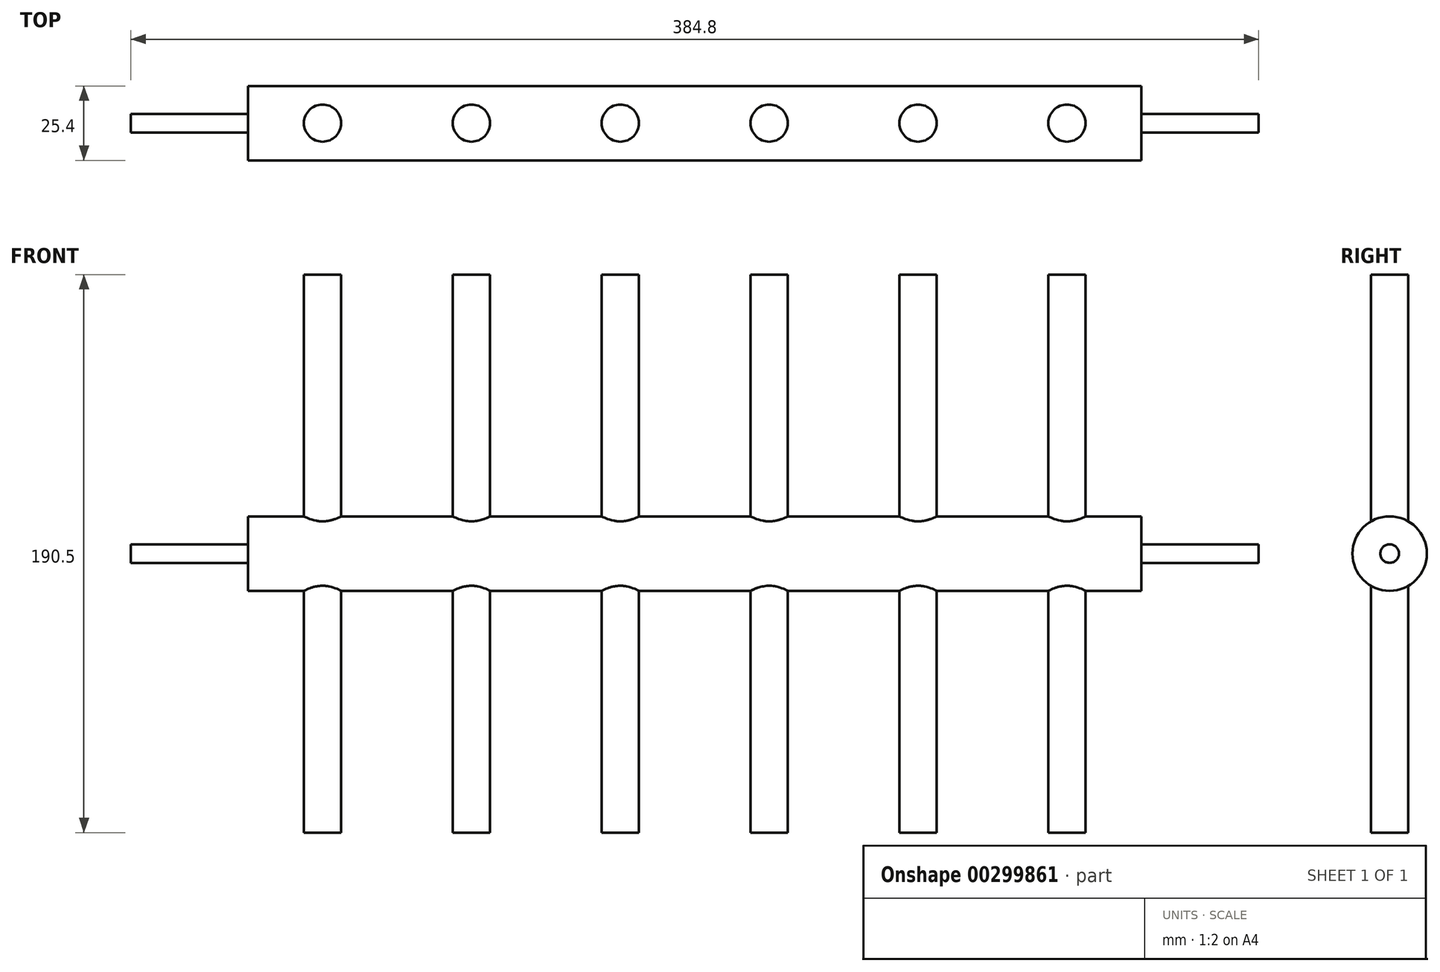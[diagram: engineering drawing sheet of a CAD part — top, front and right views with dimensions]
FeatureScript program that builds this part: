
annotation { "Feature Type Name" : "Feature", "Feature Type Description" : "" }
export const myFeature = defineFeature(function(context is Context, id is Id, definition is map)
    precondition{}
    {
        {
            var Q0;
            Q0=qCreatedBy(makeId("Right.planeOp"),FACE);
            var sketch = newSketch(context, id + "F0", { "sketchPlane" : qUnion([Q0])});
            skCircle(sketch, "E0", {"center": v(0, 0) * mm, "radius": 12.7 * mm});
            skSolve(sketch);
        }
        {
            var Q0;
            Q0=qSketchRegion(id+"F0",true);
            extrude(context, id + "F1", {"entities" : qUnion([Q0]), "depth" : 304.8 * mm});
        }
        {
            var Q0;
            Q0=makeQuery(id+"F1.opExtrude","CAP_FACE",FACE,{"disambiguationData":[OSD([sQuery(id+"F0.wireOp",EDGE,"E0")])],"isStart":false});
            var sketch = newSketch(context, id + "F2", { "sketchPlane" : qUnion([Q0])});
            skCircle(sketch, "E1", {"center": v(0, 0) * mm, "radius": 3.18 * mm});
            skSolve(sketch);
        }
        {
            var Q0;
            Q0=qSketchRegion(id+"F2",true);
            extrude(context, id + "F3", {"entities" : qUnion([Q0]), "operationType" : NewBodyOperationType.ADD, "depth" : 40 * mm});
        }
        {
            var Q0;
            Q0=makeQuery(id+"F1.opExtrude","CAP_FACE",FACE,{"disambiguationData":[OSD([sQuery(id+"F0.wireOp",EDGE,"E0")])],"isStart":true});
            var sketch = newSketch(context, id + "F4", { "sketchPlane" : qUnion([Q0])});
            skCircle(sketch, "E2", {"center": v(0, 0) * mm, "radius": 3.18 * mm});
            skSolve(sketch);
        }
        {
            var Q0;
            Q0=qSketchRegion(id+"F4",true);
            extrude(context, id + "F5", {"entities" : qUnion([Q0]), "operationType" : NewBodyOperationType.ADD, "depth" : 40 * mm});
        }
        {
            var Q0;
            Q0=qCreatedBy(makeId("Top.planeOp"),FACE);
            var sketch = newSketch(context, id + "F6", { "sketchPlane" : qUnion([Q0])});
            skCircle(sketch, "E3", {"center": v(177.8, 0) * mm, "radius": 6.35 * mm});
            skLineSegment(sketch, "E4", {"start": v(177.8, 0) * mm, "end": v(127, 0) * mm});
            skLineSegment(sketch, "E5", {"start": v(127, 0) * mm, "end": v(76.2, 0) * mm});
            skLineSegment(sketch, "E6", {"start": v(76.2, 0) * mm, "end": v(25.4, 0) * mm});
            skLineSegment(sketch, "E7", {"start": v(0, 0) * mm, "end": v(25.4, 0) * mm});
            skLineSegment(sketch, "E8", {"start": v(177.8, 0) * mm, "end": v(228.6, 0) * mm});
            skLineSegment(sketch, "E9", {"start": v(228.6, 0) * mm, "end": v(279.4, 0) * mm});
            skCircle(sketch, "E10", {"center": v(25.4, 0) * mm, "radius": 6.35 * mm});
            skCircle(sketch, "E11", {"center": v(76.2, 0) * mm, "radius": 6.35 * mm});
            skCircle(sketch, "E12", {"center": v(127, 0) * mm, "radius": 6.35 * mm});
            skCircle(sketch, "E13", {"center": v(228.6, 0) * mm, "radius": 6.35 * mm});
            skCircle(sketch, "E14", {"center": v(279.4, 0) * mm, "radius": 6.35 * mm});
            skSolve(sketch);
        }
        {
            var Q0;
            Q0=qSketchRegion(id+"F6",true);
            extrude(context, id + "F7", {"entities" : qUnion([Q0]), "operationType" : NewBodyOperationType.ADD, "depth" : 95.25 * mm, "hasSecondDirection" : true, "secondDirectionOppositeDirection" : true, "secondDirectionDepth" : 95.25 * mm});
        }
    });
